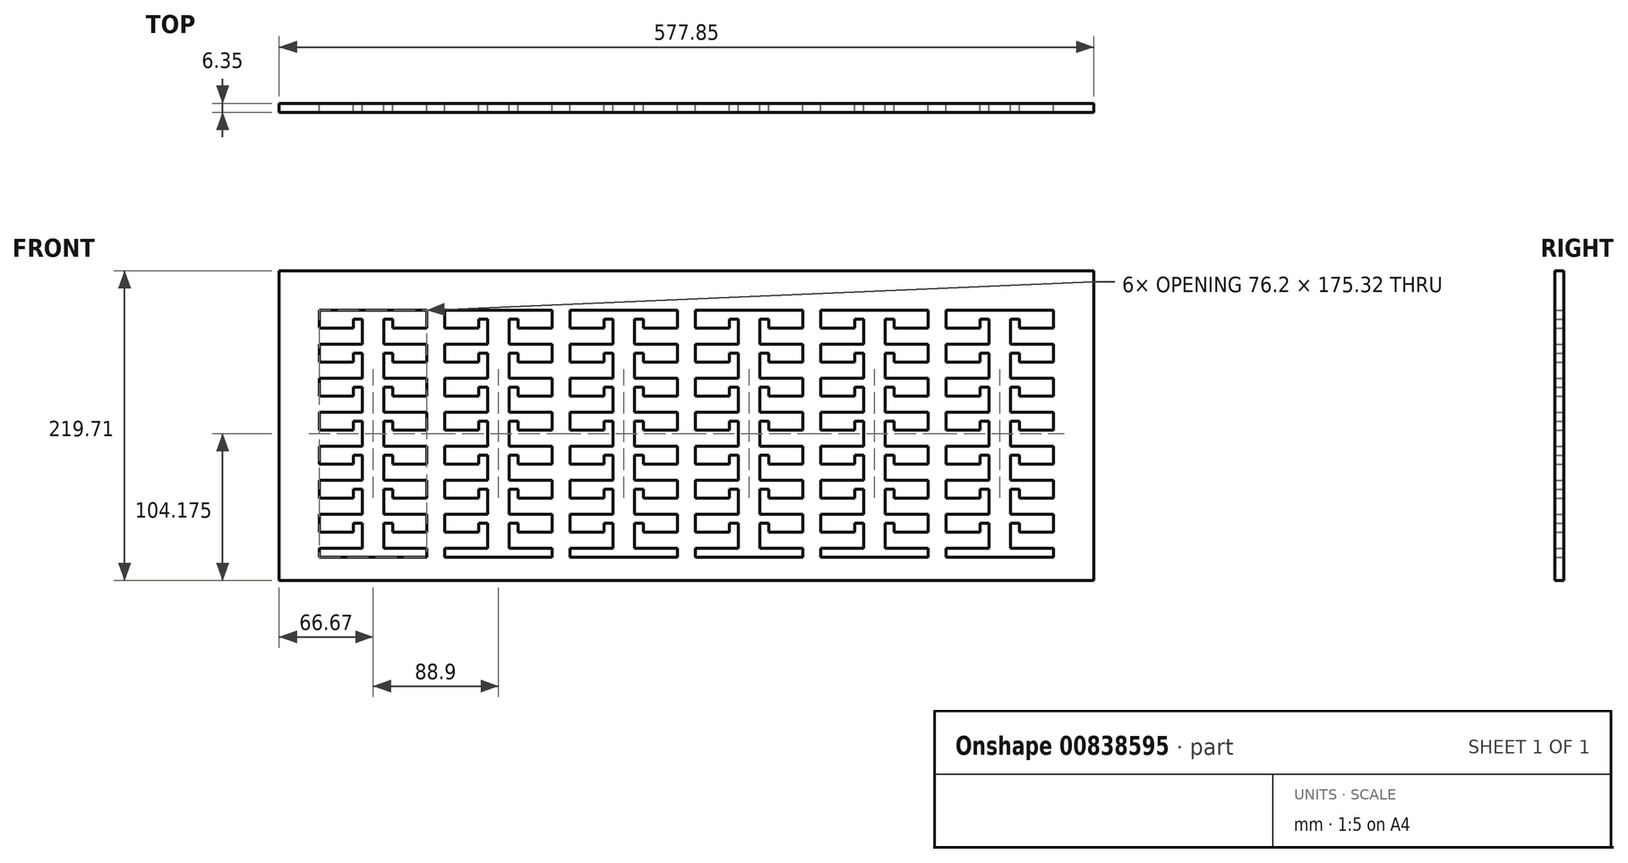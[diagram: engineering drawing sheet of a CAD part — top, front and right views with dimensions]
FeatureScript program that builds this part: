
annotation { "Feature Type Name" : "Feature", "Feature Type Description" : "" }
export const myFeature = defineFeature(function(context is Context, id is Id, definition is map)
    precondition{}
    {
        {
            var Q0;
            Q0=qCreatedBy(makeId("Front.planeOp"),FACE);
            var sketch = newSketch(context, id + "F0", { "sketchPlane" : qUnion([Q0])});
            skLineSegment(sketch, "E0", {"start": v(-97.96, -49.5) * mm, "end": v(-67.48, -49.5) * mm});
            skLineSegment(sketch, "E1", {"start": v(-67.48, -49.5) * mm, "end": v(-67.48, -31.72) * mm});
            skLineSegment(sketch, "E2", {"start": v(-67.48, -31.72) * mm, "end": v(-73.83, -31.72) * mm});
            skLineSegment(sketch, "E3", {"start": v(-73.83, -31.72) * mm, "end": v(-73.83, -38.07) * mm});
            skLineSegment(sketch, "E4", {"start": v(-73.83, -38.07) * mm, "end": v(-97.96, -38.07) * mm});
            skLineSegment(sketch, "E5", {"start": v(-97.96, -38.07) * mm, "end": v(-97.96, -25.37) * mm});
            skLineSegment(sketch, "E6", {"start": v(-97.96, -25.37) * mm, "end": v(-67.48, -25.37) * mm});
            skLineSegment(sketch, "E7", {"start": v(-67.48, -25.37) * mm, "end": v(-67.48, -7.6) * mm});
            skLineSegment(sketch, "E8", {"start": v(-67.48, -7.6) * mm, "end": v(-73.83, -7.6) * mm});
            skLineSegment(sketch, "E9", {"start": v(-73.83, -7.6) * mm, "end": v(-73.83, -13.94) * mm});
            skLineSegment(sketch, "E10", {"start": v(-73.83, -13.94) * mm, "end": v(-97.96, -13.94) * mm});
            skLineSegment(sketch, "E11", {"start": v(-97.96, -13.94) * mm, "end": v(-97.96, -1.24) * mm});
            skLineSegment(sketch, "E12", {"start": v(-97.96, -1.24) * mm, "end": v(-67.48, -1.24) * mm});
            skLineSegment(sketch, "E13", {"start": v(-67.48, -1.24) * mm, "end": v(-67.48, 16.54) * mm});
            skLineSegment(sketch, "E14", {"start": v(-67.48, 16.54) * mm, "end": v(-73.83, 16.54) * mm});
            skLineSegment(sketch, "E15", {"start": v(-73.83, 16.54) * mm, "end": v(-73.83, 10.19) * mm});
            skLineSegment(sketch, "E16", {"start": v(-73.83, 10.19) * mm, "end": v(-97.96, 10.19) * mm});
            skLineSegment(sketch, "E17", {"start": v(-97.96, 10.19) * mm, "end": v(-97.96, 22.89) * mm});
            skLineSegment(sketch, "E18", {"start": v(-97.96, 22.89) * mm, "end": v(-67.48, 22.89) * mm});
            skLineSegment(sketch, "E19", {"start": v(-67.48, 22.89) * mm, "end": v(-67.48, 40.67) * mm});
            skLineSegment(sketch, "E20", {"start": v(-67.48, 40.67) * mm, "end": v(-73.83, 40.67) * mm});
            skLineSegment(sketch, "E21", {"start": v(-73.83, 40.67) * mm, "end": v(-73.83, 34.32) * mm});
            skLineSegment(sketch, "E22", {"start": v(-73.83, 34.32) * mm, "end": v(-97.96, 34.32) * mm});
            skLineSegment(sketch, "E23", {"start": v(-97.96, 34.32) * mm, "end": v(-97.96, 47.02) * mm});
            skLineSegment(sketch, "E24", {"start": v(-21.76, -80.05) * mm, "end": v(-21.76, -73.63) * mm});
            skLineSegment(sketch, "E25", {"start": v(-21.76, -73.63) * mm, "end": v(-52.24, -73.63) * mm});
            skLineSegment(sketch, "E26", {"start": v(-52.24, -73.63) * mm, "end": v(-52.24, -55.85) * mm});
            skLineSegment(sketch, "E27", {"start": v(-52.24, -55.85) * mm, "end": v(-45.89, -55.85) * mm});
            skLineSegment(sketch, "E28", {"start": v(-45.89, -55.85) * mm, "end": v(-45.89, -62.2) * mm});
            skLineSegment(sketch, "E29", {"start": v(-45.89, -62.2) * mm, "end": v(-21.76, -62.2) * mm});
            skLineSegment(sketch, "E30", {"start": v(-21.76, -62.2) * mm, "end": v(-21.76, -49.5) * mm});
            skLineSegment(sketch, "E31", {"start": v(-21.76, -49.5) * mm, "end": v(-52.24, -49.5) * mm});
            skLineSegment(sketch, "E32", {"start": v(-52.24, -49.5) * mm, "end": v(-52.24, -31.72) * mm});
            skLineSegment(sketch, "E33", {"start": v(-52.24, -31.72) * mm, "end": v(-45.89, -31.72) * mm});
            skLineSegment(sketch, "E34", {"start": v(-45.89, -31.72) * mm, "end": v(-45.89, -38.07) * mm});
            skLineSegment(sketch, "E35", {"start": v(-45.89, -38.07) * mm, "end": v(-21.76, -38.07) * mm});
            skLineSegment(sketch, "E36", {"start": v(-21.76, -38.07) * mm, "end": v(-21.76, -25.37) * mm});
            skLineSegment(sketch, "E37", {"start": v(-21.76, -25.37) * mm, "end": v(-52.24, -25.37) * mm});
            skLineSegment(sketch, "E38", {"start": v(-52.24, -25.37) * mm, "end": v(-52.24, -7.6) * mm});
            skLineSegment(sketch, "E39", {"start": v(-52.24, -7.6) * mm, "end": v(-45.89, -7.6) * mm});
            skLineSegment(sketch, "E40", {"start": v(-45.89, -7.6) * mm, "end": v(-45.89, -13.94) * mm});
            skLineSegment(sketch, "E41", {"start": v(-45.89, -13.94) * mm, "end": v(-21.76, -13.94) * mm});
            skLineSegment(sketch, "E42", {"start": v(-21.76, -13.94) * mm, "end": v(-21.76, -1.24) * mm});
            skLineSegment(sketch, "E43", {"start": v(-21.76, -1.24) * mm, "end": v(-52.24, -1.24) * mm});
            skLineSegment(sketch, "E44", {"start": v(-52.24, -1.24) * mm, "end": v(-52.24, 16.54) * mm});
            skLineSegment(sketch, "E45", {"start": v(-52.24, 16.54) * mm, "end": v(-45.89, 16.54) * mm});
            skLineSegment(sketch, "E46", {"start": v(-45.89, 16.54) * mm, "end": v(-45.89, 10.19) * mm});
            skLineSegment(sketch, "E47", {"start": v(-45.89, 10.19) * mm, "end": v(-21.76, 10.19) * mm});
            skLineSegment(sketch, "E48", {"start": v(-21.76, 10.19) * mm, "end": v(-21.76, 22.89) * mm});
            skLineSegment(sketch, "E49", {"start": v(-21.76, 22.89) * mm, "end": v(-52.24, 22.89) * mm});
            skLineSegment(sketch, "E50", {"start": v(-52.24, 22.89) * mm, "end": v(-52.24, 40.67) * mm});
            skLineSegment(sketch, "E51", {"start": v(-52.24, 40.67) * mm, "end": v(-45.89, 40.67) * mm});
            skLineSegment(sketch, "E52", {"start": v(-45.89, 40.67) * mm, "end": v(-45.89, 34.32) * mm});
            skLineSegment(sketch, "E53", {"start": v(-45.89, 34.32) * mm, "end": v(-21.76, 34.32) * mm});
            skLineSegment(sketch, "E54", {"start": v(-21.76, 34.32) * mm, "end": v(-21.76, 47.02) * mm});
            skLineSegment(sketch, "E55", {"start": v(-67.48, -73.63) * mm, "end": v(-67.48, -55.85) * mm});
            skLineSegment(sketch, "E56", {"start": v(-73.83, -62.2) * mm, "end": v(-73.83, -55.85) * mm});
            skLineSegment(sketch, "E57", {"start": v(-73.83, -55.85) * mm, "end": v(-67.48, -55.85) * mm});
            skLineSegment(sketch, "E58", {"start": v(-67.48, -73.63) * mm, "end": v(-97.96, -73.63) * mm});
            skLineSegment(sketch, "E59", {"start": v(-97.96, -62.2) * mm, "end": v(-97.96, -49.5) * mm});
            skLineSegment(sketch, "E60", {"start": v(-97.96, -73.63) * mm, "end": v(-97.96, -80.05) * mm});
            skLineSegment(sketch, "E61", {"start": v(-97.96, -62.2) * mm, "end": v(-73.83, -62.2) * mm});
            skLineSegment(sketch, "E62", {"start": v(-97.96, -80.05) * mm, "end": v(-21.76, -80.05) * mm});
            skPoint(sketch, "E63", {"position": v(-59.86, -80.05) * mm});
            skLineSegment(sketch, "E64", {"start": v(-186.86, -49.5) * mm, "end": v(-156.38, -49.5) * mm});
            skLineSegment(sketch, "E65", {"start": v(-156.38, -49.5) * mm, "end": v(-156.38, -31.72) * mm});
            skLineSegment(sketch, "E66", {"start": v(-156.38, -31.72) * mm, "end": v(-162.73, -31.72) * mm});
            skLineSegment(sketch, "E67", {"start": v(-162.73, -31.72) * mm, "end": v(-162.73, -38.07) * mm});
            skLineSegment(sketch, "E68", {"start": v(-162.73, -38.07) * mm, "end": v(-186.86, -38.07) * mm});
            skLineSegment(sketch, "E69", {"start": v(-186.86, -38.07) * mm, "end": v(-186.86, -25.37) * mm});
            skLineSegment(sketch, "E70", {"start": v(-186.86, -25.37) * mm, "end": v(-156.38, -25.37) * mm});
            skLineSegment(sketch, "E71", {"start": v(-156.38, -25.37) * mm, "end": v(-156.38, -7.6) * mm});
            skLineSegment(sketch, "E72", {"start": v(-156.38, -7.6) * mm, "end": v(-162.73, -7.6) * mm});
            skLineSegment(sketch, "E73", {"start": v(-162.73, -7.6) * mm, "end": v(-162.73, -13.94) * mm});
            skLineSegment(sketch, "E74", {"start": v(-162.73, -13.94) * mm, "end": v(-186.86, -13.94) * mm});
            skLineSegment(sketch, "E75", {"start": v(-186.86, -13.94) * mm, "end": v(-186.86, -1.24) * mm});
            skLineSegment(sketch, "E76", {"start": v(-186.86, -1.24) * mm, "end": v(-156.38, -1.24) * mm});
            skLineSegment(sketch, "E77", {"start": v(-156.38, -1.24) * mm, "end": v(-156.38, 16.54) * mm});
            skLineSegment(sketch, "E78", {"start": v(-156.38, 16.54) * mm, "end": v(-162.73, 16.54) * mm});
            skLineSegment(sketch, "E79", {"start": v(-162.73, 16.54) * mm, "end": v(-162.73, 10.19) * mm});
            skLineSegment(sketch, "E80", {"start": v(-162.73, 10.19) * mm, "end": v(-186.86, 10.19) * mm});
            skLineSegment(sketch, "E81", {"start": v(-186.86, 10.19) * mm, "end": v(-186.86, 22.89) * mm});
            skLineSegment(sketch, "E82", {"start": v(-186.86, 22.89) * mm, "end": v(-156.38, 22.89) * mm});
            skLineSegment(sketch, "E83", {"start": v(-156.38, 22.89) * mm, "end": v(-156.38, 40.67) * mm});
            skLineSegment(sketch, "E84", {"start": v(-156.38, 40.67) * mm, "end": v(-162.73, 40.67) * mm});
            skLineSegment(sketch, "E85", {"start": v(-162.73, 40.67) * mm, "end": v(-162.73, 34.32) * mm});
            skLineSegment(sketch, "E86", {"start": v(-162.73, 34.32) * mm, "end": v(-186.86, 34.32) * mm});
            skLineSegment(sketch, "E87", {"start": v(-186.86, 34.32) * mm, "end": v(-186.86, 47.02) * mm});
            skLineSegment(sketch, "E88", {"start": v(-110.66, -80.05) * mm, "end": v(-110.66, -73.63) * mm});
            skLineSegment(sketch, "E89", {"start": v(-110.66, -73.63) * mm, "end": v(-141.14, -73.63) * mm});
            skLineSegment(sketch, "E90", {"start": v(-141.14, -73.63) * mm, "end": v(-141.14, -55.85) * mm});
            skLineSegment(sketch, "E91", {"start": v(-141.14, -55.85) * mm, "end": v(-134.79, -55.85) * mm});
            skLineSegment(sketch, "E92", {"start": v(-134.79, -55.85) * mm, "end": v(-134.79, -62.2) * mm});
            skLineSegment(sketch, "E93", {"start": v(-134.79, -62.2) * mm, "end": v(-110.66, -62.2) * mm});
            skLineSegment(sketch, "E94", {"start": v(-110.66, -62.2) * mm, "end": v(-110.66, -49.5) * mm});
            skLineSegment(sketch, "E95", {"start": v(-110.66, -49.5) * mm, "end": v(-141.14, -49.5) * mm});
            skLineSegment(sketch, "E96", {"start": v(-141.14, -49.5) * mm, "end": v(-141.14, -31.72) * mm});
            skLineSegment(sketch, "E97", {"start": v(-141.14, -31.72) * mm, "end": v(-134.79, -31.72) * mm});
            skLineSegment(sketch, "E98", {"start": v(-134.79, -31.72) * mm, "end": v(-134.79, -38.07) * mm});
            skLineSegment(sketch, "E99", {"start": v(-134.79, -38.07) * mm, "end": v(-110.66, -38.07) * mm});
            skLineSegment(sketch, "E100", {"start": v(-110.66, -38.07) * mm, "end": v(-110.66, -25.37) * mm});
            skLineSegment(sketch, "E101", {"start": v(-110.66, -25.37) * mm, "end": v(-141.14, -25.37) * mm});
            skLineSegment(sketch, "E102", {"start": v(-141.14, -25.37) * mm, "end": v(-141.14, -7.6) * mm});
            skLineSegment(sketch, "E103", {"start": v(-141.14, -7.6) * mm, "end": v(-134.79, -7.6) * mm});
            skLineSegment(sketch, "E104", {"start": v(-134.79, -7.6) * mm, "end": v(-134.79, -13.94) * mm});
            skLineSegment(sketch, "E105", {"start": v(-134.79, -13.94) * mm, "end": v(-110.66, -13.94) * mm});
            skLineSegment(sketch, "E106", {"start": v(-110.66, -13.94) * mm, "end": v(-110.66, -1.24) * mm});
            skLineSegment(sketch, "E107", {"start": v(-110.66, -1.24) * mm, "end": v(-141.14, -1.24) * mm});
            skLineSegment(sketch, "E108", {"start": v(-141.14, -1.24) * mm, "end": v(-141.14, 16.54) * mm});
            skLineSegment(sketch, "E109", {"start": v(-141.14, 16.54) * mm, "end": v(-134.79, 16.54) * mm});
            skLineSegment(sketch, "E110", {"start": v(-134.79, 16.54) * mm, "end": v(-134.79, 10.19) * mm});
            skLineSegment(sketch, "E111", {"start": v(-134.79, 10.19) * mm, "end": v(-110.66, 10.19) * mm});
            skLineSegment(sketch, "E112", {"start": v(-110.66, 10.19) * mm, "end": v(-110.66, 22.89) * mm});
            skLineSegment(sketch, "E113", {"start": v(-110.66, 22.89) * mm, "end": v(-141.14, 22.89) * mm});
            skLineSegment(sketch, "E114", {"start": v(-141.14, 22.89) * mm, "end": v(-141.14, 40.67) * mm});
            skLineSegment(sketch, "E115", {"start": v(-141.14, 40.67) * mm, "end": v(-134.79, 40.67) * mm});
            skLineSegment(sketch, "E116", {"start": v(-134.79, 40.67) * mm, "end": v(-134.79, 34.32) * mm});
            skLineSegment(sketch, "E117", {"start": v(-134.79, 34.32) * mm, "end": v(-110.66, 34.32) * mm});
            skLineSegment(sketch, "E118", {"start": v(-110.66, 34.32) * mm, "end": v(-110.66, 47.02) * mm});
            skLineSegment(sketch, "E119", {"start": v(-156.38, -73.63) * mm, "end": v(-156.38, -55.85) * mm});
            skLineSegment(sketch, "E120", {"start": v(-162.73, -62.2) * mm, "end": v(-162.73, -55.85) * mm});
            skLineSegment(sketch, "E121", {"start": v(-162.73, -55.85) * mm, "end": v(-156.38, -55.85) * mm});
            skLineSegment(sketch, "E122", {"start": v(-156.38, -73.63) * mm, "end": v(-186.86, -73.63) * mm});
            skLineSegment(sketch, "E123", {"start": v(-186.86, -62.2) * mm, "end": v(-186.86, -49.5) * mm});
            skLineSegment(sketch, "E124", {"start": v(-186.86, -73.63) * mm, "end": v(-186.86, -80.05) * mm});
            skLineSegment(sketch, "E125", {"start": v(-186.86, -62.2) * mm, "end": v(-162.73, -62.2) * mm});
            skLineSegment(sketch, "E126", {"start": v(-186.86, -80.05) * mm, "end": v(-110.66, -80.05) * mm});
            skPoint(sketch, "E127", {"position": v(-148.76, -80.05) * mm});
            skLineSegment(sketch, "E128", {"start": v(-275.76, -49.5) * mm, "end": v(-245.28, -49.5) * mm});
            skLineSegment(sketch, "E129", {"start": v(-245.28, -49.5) * mm, "end": v(-245.28, -31.72) * mm});
            skLineSegment(sketch, "E130", {"start": v(-245.28, -31.72) * mm, "end": v(-251.63, -31.72) * mm});
            skLineSegment(sketch, "E131", {"start": v(-251.63, -31.72) * mm, "end": v(-251.63, -38.07) * mm});
            skLineSegment(sketch, "E132", {"start": v(-251.63, -38.07) * mm, "end": v(-275.76, -38.07) * mm});
            skLineSegment(sketch, "E133", {"start": v(-275.76, -38.07) * mm, "end": v(-275.76, -25.37) * mm});
            skLineSegment(sketch, "E134", {"start": v(-275.76, -25.37) * mm, "end": v(-245.28, -25.37) * mm});
            skLineSegment(sketch, "E135", {"start": v(-245.28, -25.37) * mm, "end": v(-245.28, -7.6) * mm});
            skLineSegment(sketch, "E136", {"start": v(-245.28, -7.6) * mm, "end": v(-251.63, -7.6) * mm});
            skLineSegment(sketch, "E137", {"start": v(-251.63, -7.6) * mm, "end": v(-251.63, -13.94) * mm});
            skLineSegment(sketch, "E138", {"start": v(-251.63, -13.94) * mm, "end": v(-275.76, -13.94) * mm});
            skLineSegment(sketch, "E139", {"start": v(-275.76, -13.94) * mm, "end": v(-275.76, -1.24) * mm});
            skLineSegment(sketch, "E140", {"start": v(-275.76, -1.24) * mm, "end": v(-245.28, -1.24) * mm});
            skLineSegment(sketch, "E141", {"start": v(-245.28, -1.24) * mm, "end": v(-245.28, 16.54) * mm});
            skLineSegment(sketch, "E142", {"start": v(-245.28, 16.54) * mm, "end": v(-251.63, 16.54) * mm});
            skLineSegment(sketch, "E143", {"start": v(-251.63, 16.54) * mm, "end": v(-251.63, 10.19) * mm});
            skLineSegment(sketch, "E144", {"start": v(-251.63, 10.19) * mm, "end": v(-275.76, 10.19) * mm});
            skLineSegment(sketch, "E145", {"start": v(-275.76, 10.19) * mm, "end": v(-275.76, 22.89) * mm});
            skLineSegment(sketch, "E146", {"start": v(-275.76, 22.89) * mm, "end": v(-245.28, 22.89) * mm});
            skLineSegment(sketch, "E147", {"start": v(-245.28, 22.89) * mm, "end": v(-245.28, 40.67) * mm});
            skLineSegment(sketch, "E148", {"start": v(-245.28, 40.67) * mm, "end": v(-251.63, 40.67) * mm});
            skLineSegment(sketch, "E149", {"start": v(-251.63, 40.67) * mm, "end": v(-251.63, 34.32) * mm});
            skLineSegment(sketch, "E150", {"start": v(-251.63, 34.32) * mm, "end": v(-275.76, 34.32) * mm});
            skLineSegment(sketch, "E151", {"start": v(-275.76, 34.32) * mm, "end": v(-275.76, 47.02) * mm});
            skLineSegment(sketch, "E152", {"start": v(-199.56, -80.05) * mm, "end": v(-199.56, -73.63) * mm});
            skLineSegment(sketch, "E153", {"start": v(-199.56, -73.63) * mm, "end": v(-230.04, -73.63) * mm});
            skLineSegment(sketch, "E154", {"start": v(-230.04, -73.63) * mm, "end": v(-230.04, -55.85) * mm});
            skLineSegment(sketch, "E155", {"start": v(-230.04, -55.85) * mm, "end": v(-223.69, -55.85) * mm});
            skLineSegment(sketch, "E156", {"start": v(-223.69, -55.85) * mm, "end": v(-223.69, -62.2) * mm});
            skLineSegment(sketch, "E157", {"start": v(-223.69, -62.2) * mm, "end": v(-199.56, -62.2) * mm});
            skLineSegment(sketch, "E158", {"start": v(-199.56, -62.2) * mm, "end": v(-199.56, -49.5) * mm});
            skLineSegment(sketch, "E159", {"start": v(-199.56, -49.5) * mm, "end": v(-230.04, -49.5) * mm});
            skLineSegment(sketch, "E160", {"start": v(-230.04, -49.5) * mm, "end": v(-230.04, -31.72) * mm});
            skLineSegment(sketch, "E161", {"start": v(-230.04, -31.72) * mm, "end": v(-223.69, -31.72) * mm});
            skLineSegment(sketch, "E162", {"start": v(-223.69, -31.72) * mm, "end": v(-223.69, -38.07) * mm});
            skLineSegment(sketch, "E163", {"start": v(-223.69, -38.07) * mm, "end": v(-199.56, -38.07) * mm});
            skLineSegment(sketch, "E164", {"start": v(-199.56, -38.07) * mm, "end": v(-199.56, -25.37) * mm});
            skLineSegment(sketch, "E165", {"start": v(-199.56, -25.37) * mm, "end": v(-230.04, -25.37) * mm});
            skLineSegment(sketch, "E166", {"start": v(-230.04, -25.37) * mm, "end": v(-230.04, -7.6) * mm});
            skLineSegment(sketch, "E167", {"start": v(-230.04, -7.6) * mm, "end": v(-223.69, -7.6) * mm});
            skLineSegment(sketch, "E168", {"start": v(-223.69, -7.6) * mm, "end": v(-223.69, -13.94) * mm});
            skLineSegment(sketch, "E169", {"start": v(-223.69, -13.94) * mm, "end": v(-199.56, -13.94) * mm});
            skLineSegment(sketch, "E170", {"start": v(-199.56, -13.94) * mm, "end": v(-199.56, -1.24) * mm});
            skLineSegment(sketch, "E171", {"start": v(-199.56, -1.24) * mm, "end": v(-230.04, -1.24) * mm});
            skLineSegment(sketch, "E172", {"start": v(-230.04, -1.24) * mm, "end": v(-230.04, 16.54) * mm});
            skLineSegment(sketch, "E173", {"start": v(-230.04, 16.54) * mm, "end": v(-223.69, 16.54) * mm});
            skLineSegment(sketch, "E174", {"start": v(-223.69, 16.54) * mm, "end": v(-223.69, 10.19) * mm});
            skLineSegment(sketch, "E175", {"start": v(-223.69, 10.19) * mm, "end": v(-199.56, 10.19) * mm});
            skLineSegment(sketch, "E176", {"start": v(-199.56, 10.19) * mm, "end": v(-199.56, 22.89) * mm});
            skLineSegment(sketch, "E177", {"start": v(-199.56, 22.89) * mm, "end": v(-230.04, 22.89) * mm});
            skLineSegment(sketch, "E178", {"start": v(-230.04, 22.89) * mm, "end": v(-230.04, 40.67) * mm});
            skLineSegment(sketch, "E179", {"start": v(-230.04, 40.67) * mm, "end": v(-223.69, 40.67) * mm});
            skLineSegment(sketch, "E180", {"start": v(-223.69, 40.67) * mm, "end": v(-223.69, 34.32) * mm});
            skLineSegment(sketch, "E181", {"start": v(-223.69, 34.32) * mm, "end": v(-199.56, 34.32) * mm});
            skLineSegment(sketch, "E182", {"start": v(-199.56, 34.32) * mm, "end": v(-199.56, 47.02) * mm});
            skLineSegment(sketch, "E183", {"start": v(-245.28, -73.63) * mm, "end": v(-245.28, -55.85) * mm});
            skLineSegment(sketch, "E184", {"start": v(-251.63, -62.2) * mm, "end": v(-251.63, -55.85) * mm});
            skLineSegment(sketch, "E185", {"start": v(-251.63, -55.85) * mm, "end": v(-245.28, -55.85) * mm});
            skLineSegment(sketch, "E186", {"start": v(-245.28, -73.63) * mm, "end": v(-275.76, -73.63) * mm});
            skLineSegment(sketch, "E187", {"start": v(-275.76, -62.2) * mm, "end": v(-275.76, -49.5) * mm});
            skLineSegment(sketch, "E188", {"start": v(-275.76, -73.63) * mm, "end": v(-275.76, -80.05) * mm});
            skLineSegment(sketch, "E189", {"start": v(-275.76, -62.2) * mm, "end": v(-251.63, -62.2) * mm});
            skLineSegment(sketch, "E190", {"start": v(-275.76, -80.05) * mm, "end": v(-199.56, -80.05) * mm});
            skPoint(sketch, "E191", {"position": v(-237.66, -80.05) * mm});
            skLineSegment(sketch, "E192", {"start": v(-364.66, -49.5) * mm, "end": v(-334.18, -49.5) * mm});
            skLineSegment(sketch, "E193", {"start": v(-334.18, -49.5) * mm, "end": v(-334.18, -31.72) * mm});
            skLineSegment(sketch, "E194", {"start": v(-334.18, -31.72) * mm, "end": v(-340.53, -31.72) * mm});
            skLineSegment(sketch, "E195", {"start": v(-340.53, -31.72) * mm, "end": v(-340.53, -38.07) * mm});
            skLineSegment(sketch, "E196", {"start": v(-340.53, -38.07) * mm, "end": v(-364.66, -38.07) * mm});
            skLineSegment(sketch, "E197", {"start": v(-364.66, -38.07) * mm, "end": v(-364.66, -25.37) * mm});
            skLineSegment(sketch, "E198", {"start": v(-364.66, -25.37) * mm, "end": v(-334.18, -25.37) * mm});
            skLineSegment(sketch, "E199", {"start": v(-334.18, -25.37) * mm, "end": v(-334.18, -7.6) * mm});
            skLineSegment(sketch, "E200", {"start": v(-334.18, -7.6) * mm, "end": v(-340.53, -7.6) * mm});
            skLineSegment(sketch, "E201", {"start": v(-340.53, -7.6) * mm, "end": v(-340.53, -13.94) * mm});
            skLineSegment(sketch, "E202", {"start": v(-340.53, -13.94) * mm, "end": v(-364.66, -13.94) * mm});
            skLineSegment(sketch, "E203", {"start": v(-364.66, -13.94) * mm, "end": v(-364.66, -1.24) * mm});
            skLineSegment(sketch, "E204", {"start": v(-364.66, -1.24) * mm, "end": v(-334.18, -1.24) * mm});
            skLineSegment(sketch, "E205", {"start": v(-334.18, -1.24) * mm, "end": v(-334.18, 16.54) * mm});
            skLineSegment(sketch, "E206", {"start": v(-334.18, 16.54) * mm, "end": v(-340.53, 16.54) * mm});
            skLineSegment(sketch, "E207", {"start": v(-340.53, 16.54) * mm, "end": v(-340.53, 10.19) * mm});
            skLineSegment(sketch, "E208", {"start": v(-340.53, 10.19) * mm, "end": v(-364.66, 10.19) * mm});
            skLineSegment(sketch, "E209", {"start": v(-364.66, 10.19) * mm, "end": v(-364.66, 22.89) * mm});
            skLineSegment(sketch, "E210", {"start": v(-364.66, 22.89) * mm, "end": v(-334.18, 22.89) * mm});
            skLineSegment(sketch, "E211", {"start": v(-334.18, 22.89) * mm, "end": v(-334.18, 40.67) * mm});
            skLineSegment(sketch, "E212", {"start": v(-334.18, 40.67) * mm, "end": v(-340.53, 40.67) * mm});
            skLineSegment(sketch, "E213", {"start": v(-340.53, 40.67) * mm, "end": v(-340.53, 34.32) * mm});
            skLineSegment(sketch, "E214", {"start": v(-340.53, 34.32) * mm, "end": v(-364.66, 34.32) * mm});
            skLineSegment(sketch, "E215", {"start": v(-364.66, 34.32) * mm, "end": v(-364.66, 47.02) * mm});
            skLineSegment(sketch, "E216", {"start": v(-288.46, -80.05) * mm, "end": v(-288.46, -73.63) * mm});
            skLineSegment(sketch, "E217", {"start": v(-288.46, -73.63) * mm, "end": v(-318.94, -73.63) * mm});
            skLineSegment(sketch, "E218", {"start": v(-318.94, -73.63) * mm, "end": v(-318.94, -55.85) * mm});
            skLineSegment(sketch, "E219", {"start": v(-318.94, -55.85) * mm, "end": v(-312.59, -55.85) * mm});
            skLineSegment(sketch, "E220", {"start": v(-312.59, -55.85) * mm, "end": v(-312.59, -62.2) * mm});
            skLineSegment(sketch, "E221", {"start": v(-312.59, -62.2) * mm, "end": v(-288.46, -62.2) * mm});
            skLineSegment(sketch, "E222", {"start": v(-288.46, -62.2) * mm, "end": v(-288.46, -49.5) * mm});
            skLineSegment(sketch, "E223", {"start": v(-288.46, -49.5) * mm, "end": v(-318.94, -49.5) * mm});
            skLineSegment(sketch, "E224", {"start": v(-318.94, -49.5) * mm, "end": v(-318.94, -31.72) * mm});
            skLineSegment(sketch, "E225", {"start": v(-318.94, -31.72) * mm, "end": v(-312.59, -31.72) * mm});
            skLineSegment(sketch, "E226", {"start": v(-312.59, -31.72) * mm, "end": v(-312.59, -38.07) * mm});
            skLineSegment(sketch, "E227", {"start": v(-312.59, -38.07) * mm, "end": v(-288.46, -38.07) * mm});
            skLineSegment(sketch, "E228", {"start": v(-288.46, -38.07) * mm, "end": v(-288.46, -25.37) * mm});
            skLineSegment(sketch, "E229", {"start": v(-288.46, -25.37) * mm, "end": v(-318.94, -25.37) * mm});
            skLineSegment(sketch, "E230", {"start": v(-318.94, -25.37) * mm, "end": v(-318.94, -7.6) * mm});
            skLineSegment(sketch, "E231", {"start": v(-318.94, -7.6) * mm, "end": v(-312.59, -7.6) * mm});
            skLineSegment(sketch, "E232", {"start": v(-312.59, -7.6) * mm, "end": v(-312.59, -13.94) * mm});
            skLineSegment(sketch, "E233", {"start": v(-312.59, -13.94) * mm, "end": v(-288.46, -13.94) * mm});
            skLineSegment(sketch, "E234", {"start": v(-288.46, -13.94) * mm, "end": v(-288.46, -1.24) * mm});
            skLineSegment(sketch, "E235", {"start": v(-288.46, -1.24) * mm, "end": v(-318.94, -1.24) * mm});
            skLineSegment(sketch, "E236", {"start": v(-318.94, -1.24) * mm, "end": v(-318.94, 16.54) * mm});
            skLineSegment(sketch, "E237", {"start": v(-318.94, 16.54) * mm, "end": v(-312.59, 16.54) * mm});
            skLineSegment(sketch, "E238", {"start": v(-312.59, 16.54) * mm, "end": v(-312.59, 10.19) * mm});
            skLineSegment(sketch, "E239", {"start": v(-312.59, 10.19) * mm, "end": v(-288.46, 10.19) * mm});
            skLineSegment(sketch, "E240", {"start": v(-288.46, 10.19) * mm, "end": v(-288.46, 22.89) * mm});
            skLineSegment(sketch, "E241", {"start": v(-288.46, 22.89) * mm, "end": v(-318.94, 22.89) * mm});
            skLineSegment(sketch, "E242", {"start": v(-318.94, 22.89) * mm, "end": v(-318.94, 40.67) * mm});
            skLineSegment(sketch, "E243", {"start": v(-318.94, 40.67) * mm, "end": v(-312.59, 40.67) * mm});
            skLineSegment(sketch, "E244", {"start": v(-312.59, 40.67) * mm, "end": v(-312.59, 34.32) * mm});
            skLineSegment(sketch, "E245", {"start": v(-312.59, 34.32) * mm, "end": v(-288.46, 34.32) * mm});
            skLineSegment(sketch, "E246", {"start": v(-288.46, 34.32) * mm, "end": v(-288.46, 47.02) * mm});
            skLineSegment(sketch, "E247", {"start": v(-334.18, -73.63) * mm, "end": v(-334.18, -55.85) * mm});
            skLineSegment(sketch, "E248", {"start": v(-340.53, -62.2) * mm, "end": v(-340.53, -55.85) * mm});
            skLineSegment(sketch, "E249", {"start": v(-340.53, -55.85) * mm, "end": v(-334.18, -55.85) * mm});
            skLineSegment(sketch, "E250", {"start": v(-334.18, -73.63) * mm, "end": v(-364.66, -73.63) * mm});
            skLineSegment(sketch, "E251", {"start": v(-364.66, -62.2) * mm, "end": v(-364.66, -49.5) * mm});
            skLineSegment(sketch, "E252", {"start": v(-364.66, -73.63) * mm, "end": v(-364.66, -80.05) * mm});
            skLineSegment(sketch, "E253", {"start": v(-364.66, -62.2) * mm, "end": v(-340.53, -62.2) * mm});
            skLineSegment(sketch, "E254", {"start": v(-364.66, -80.05) * mm, "end": v(-288.46, -80.05) * mm});
            skPoint(sketch, "E255", {"position": v(-326.56, -80.05) * mm});
            skLineSegment(sketch, "E256.bottom", {"start": v(6.82, 123.15) * mm, "end": v(-571.03, 123.15) * mm});
            skLineSegment(sketch, "E256.top", {"start": v(6.82, -96.56) * mm, "end": v(-571.03, -96.56) * mm});
            skLineSegment(sketch, "E256.left", {"start": v(6.82, 123.15) * mm, "end": v(6.82, -96.56) * mm});
            skLineSegment(sketch, "E256.right", {"start": v(-571.03, 123.15) * mm, "end": v(-571.03, -96.56) * mm});
            skPoint(sketch, "E257", {"position": v(-282.1, 123.15) * mm});
            skLineSegment(sketch, "E258", {"start": v(-453.56, -49.5) * mm, "end": v(-423.08, -49.5) * mm});
            skLineSegment(sketch, "E259", {"start": v(-423.08, -49.5) * mm, "end": v(-423.08, -31.72) * mm});
            skLineSegment(sketch, "E260", {"start": v(-423.08, -31.72) * mm, "end": v(-429.43, -31.72) * mm});
            skLineSegment(sketch, "E261", {"start": v(-429.43, -31.72) * mm, "end": v(-429.43, -38.07) * mm});
            skLineSegment(sketch, "E262", {"start": v(-429.43, -38.07) * mm, "end": v(-453.56, -38.07) * mm});
            skLineSegment(sketch, "E263", {"start": v(-453.56, -38.07) * mm, "end": v(-453.56, -25.37) * mm});
            skLineSegment(sketch, "E264", {"start": v(-453.56, -25.37) * mm, "end": v(-423.08, -25.37) * mm});
            skLineSegment(sketch, "E265", {"start": v(-423.08, -25.37) * mm, "end": v(-423.08, -7.6) * mm});
            skLineSegment(sketch, "E266", {"start": v(-423.08, -7.6) * mm, "end": v(-429.43, -7.6) * mm});
            skLineSegment(sketch, "E267", {"start": v(-429.43, -7.6) * mm, "end": v(-429.43, -13.94) * mm});
            skLineSegment(sketch, "E268", {"start": v(-429.43, -13.94) * mm, "end": v(-453.56, -13.94) * mm});
            skLineSegment(sketch, "E269", {"start": v(-453.56, -13.94) * mm, "end": v(-453.56, -1.24) * mm});
            skLineSegment(sketch, "E270", {"start": v(-453.56, -1.24) * mm, "end": v(-423.08, -1.24) * mm});
            skLineSegment(sketch, "E271", {"start": v(-423.08, -1.24) * mm, "end": v(-423.08, 16.54) * mm});
            skLineSegment(sketch, "E272", {"start": v(-423.08, 16.54) * mm, "end": v(-429.43, 16.54) * mm});
            skLineSegment(sketch, "E273", {"start": v(-429.43, 16.54) * mm, "end": v(-429.43, 10.19) * mm});
            skLineSegment(sketch, "E274", {"start": v(-429.43, 10.19) * mm, "end": v(-453.56, 10.19) * mm});
            skLineSegment(sketch, "E275", {"start": v(-453.56, 10.19) * mm, "end": v(-453.56, 22.89) * mm});
            skLineSegment(sketch, "E276", {"start": v(-453.56, 22.89) * mm, "end": v(-423.08, 22.89) * mm});
            skLineSegment(sketch, "E277", {"start": v(-423.08, 22.89) * mm, "end": v(-423.08, 40.67) * mm});
            skLineSegment(sketch, "E278", {"start": v(-423.08, 40.67) * mm, "end": v(-429.43, 40.67) * mm});
            skLineSegment(sketch, "E279", {"start": v(-429.43, 40.67) * mm, "end": v(-429.43, 34.32) * mm});
            skLineSegment(sketch, "E280", {"start": v(-429.43, 34.32) * mm, "end": v(-453.56, 34.32) * mm});
            skLineSegment(sketch, "E281", {"start": v(-453.56, 34.32) * mm, "end": v(-453.56, 47.02) * mm});
            skLineSegment(sketch, "E282", {"start": v(-377.36, -80.05) * mm, "end": v(-377.36, -73.63) * mm});
            skLineSegment(sketch, "E283", {"start": v(-377.36, -73.63) * mm, "end": v(-407.84, -73.63) * mm});
            skLineSegment(sketch, "E284", {"start": v(-407.84, -73.63) * mm, "end": v(-407.84, -55.85) * mm});
            skLineSegment(sketch, "E285", {"start": v(-407.84, -55.85) * mm, "end": v(-401.49, -55.85) * mm});
            skLineSegment(sketch, "E286", {"start": v(-401.49, -55.85) * mm, "end": v(-401.49, -62.2) * mm});
            skLineSegment(sketch, "E287", {"start": v(-401.49, -62.2) * mm, "end": v(-377.36, -62.2) * mm});
            skLineSegment(sketch, "E288", {"start": v(-377.36, -62.2) * mm, "end": v(-377.36, -49.5) * mm});
            skLineSegment(sketch, "E289", {"start": v(-377.36, -49.5) * mm, "end": v(-407.84, -49.5) * mm});
            skLineSegment(sketch, "E290", {"start": v(-407.84, -49.5) * mm, "end": v(-407.84, -31.72) * mm});
            skLineSegment(sketch, "E291", {"start": v(-407.84, -31.72) * mm, "end": v(-401.49, -31.72) * mm});
            skLineSegment(sketch, "E292", {"start": v(-401.49, -31.72) * mm, "end": v(-401.49, -38.07) * mm});
            skLineSegment(sketch, "E293", {"start": v(-401.49, -38.07) * mm, "end": v(-377.36, -38.07) * mm});
            skLineSegment(sketch, "E294", {"start": v(-377.36, -38.07) * mm, "end": v(-377.36, -25.37) * mm});
            skLineSegment(sketch, "E295", {"start": v(-377.36, -25.37) * mm, "end": v(-407.84, -25.37) * mm});
            skLineSegment(sketch, "E296", {"start": v(-407.84, -25.37) * mm, "end": v(-407.84, -7.6) * mm});
            skLineSegment(sketch, "E297", {"start": v(-407.84, -7.6) * mm, "end": v(-401.49, -7.6) * mm});
            skLineSegment(sketch, "E298", {"start": v(-401.49, -7.6) * mm, "end": v(-401.49, -13.94) * mm});
            skLineSegment(sketch, "E299", {"start": v(-401.49, -13.94) * mm, "end": v(-377.36, -13.94) * mm});
            skLineSegment(sketch, "E300", {"start": v(-377.36, -13.94) * mm, "end": v(-377.36, -1.24) * mm});
            skLineSegment(sketch, "E301", {"start": v(-377.36, -1.24) * mm, "end": v(-407.84, -1.24) * mm});
            skLineSegment(sketch, "E302", {"start": v(-407.84, -1.24) * mm, "end": v(-407.84, 16.54) * mm});
            skLineSegment(sketch, "E303", {"start": v(-407.84, 16.54) * mm, "end": v(-401.49, 16.54) * mm});
            skLineSegment(sketch, "E304", {"start": v(-401.49, 16.54) * mm, "end": v(-401.49, 10.19) * mm});
            skLineSegment(sketch, "E305", {"start": v(-401.49, 10.19) * mm, "end": v(-377.36, 10.19) * mm});
            skLineSegment(sketch, "E306", {"start": v(-377.36, 10.19) * mm, "end": v(-377.36, 22.89) * mm});
            skLineSegment(sketch, "E307", {"start": v(-377.36, 22.89) * mm, "end": v(-407.84, 22.89) * mm});
            skLineSegment(sketch, "E308", {"start": v(-407.84, 22.89) * mm, "end": v(-407.84, 40.67) * mm});
            skLineSegment(sketch, "E309", {"start": v(-407.84, 40.67) * mm, "end": v(-401.49, 40.67) * mm});
            skLineSegment(sketch, "E310", {"start": v(-401.49, 40.67) * mm, "end": v(-401.49, 34.32) * mm});
            skLineSegment(sketch, "E311", {"start": v(-401.49, 34.32) * mm, "end": v(-377.36, 34.32) * mm});
            skLineSegment(sketch, "E312", {"start": v(-377.36, 34.32) * mm, "end": v(-377.36, 47.02) * mm});
            skLineSegment(sketch, "E313", {"start": v(-423.08, -73.63) * mm, "end": v(-423.08, -55.85) * mm});
            skLineSegment(sketch, "E314", {"start": v(-429.43, -62.2) * mm, "end": v(-429.43, -55.85) * mm});
            skLineSegment(sketch, "E315", {"start": v(-429.43, -55.85) * mm, "end": v(-423.08, -55.85) * mm});
            skLineSegment(sketch, "E316", {"start": v(-423.08, -73.63) * mm, "end": v(-453.56, -73.63) * mm});
            skLineSegment(sketch, "E317", {"start": v(-453.56, -62.2) * mm, "end": v(-453.56, -49.5) * mm});
            skLineSegment(sketch, "E318", {"start": v(-453.56, -73.63) * mm, "end": v(-453.56, -80.05) * mm});
            skLineSegment(sketch, "E319", {"start": v(-453.56, -62.2) * mm, "end": v(-429.43, -62.2) * mm});
            skLineSegment(sketch, "E320", {"start": v(-453.56, -80.05) * mm, "end": v(-377.36, -80.05) * mm});
            skPoint(sketch, "E321", {"position": v(-415.46, -80.05) * mm});
            skLineSegment(sketch, "E322", {"start": v(-542.46, -49.5) * mm, "end": v(-511.98, -49.5) * mm});
            skLineSegment(sketch, "E323", {"start": v(-511.98, -49.5) * mm, "end": v(-511.98, -31.72) * mm});
            skLineSegment(sketch, "E324", {"start": v(-511.98, -31.72) * mm, "end": v(-518.33, -31.72) * mm});
            skLineSegment(sketch, "E325", {"start": v(-518.33, -31.72) * mm, "end": v(-518.33, -38.07) * mm});
            skLineSegment(sketch, "E326", {"start": v(-518.33, -38.07) * mm, "end": v(-542.46, -38.07) * mm});
            skLineSegment(sketch, "E327", {"start": v(-542.46, -38.07) * mm, "end": v(-542.46, -25.37) * mm});
            skLineSegment(sketch, "E328", {"start": v(-542.46, -25.37) * mm, "end": v(-511.98, -25.37) * mm});
            skLineSegment(sketch, "E329", {"start": v(-511.98, -25.37) * mm, "end": v(-511.98, -7.6) * mm});
            skLineSegment(sketch, "E330", {"start": v(-511.98, -7.6) * mm, "end": v(-518.33, -7.6) * mm});
            skLineSegment(sketch, "E331", {"start": v(-518.33, -7.6) * mm, "end": v(-518.33, -13.94) * mm});
            skLineSegment(sketch, "E332", {"start": v(-518.33, -13.94) * mm, "end": v(-542.46, -13.94) * mm});
            skLineSegment(sketch, "E333", {"start": v(-542.46, -13.94) * mm, "end": v(-542.46, -1.24) * mm});
            skLineSegment(sketch, "E334", {"start": v(-542.46, -1.24) * mm, "end": v(-511.98, -1.24) * mm});
            skLineSegment(sketch, "E335", {"start": v(-511.98, -1.24) * mm, "end": v(-511.98, 16.54) * mm});
            skLineSegment(sketch, "E336", {"start": v(-511.98, 16.54) * mm, "end": v(-518.33, 16.54) * mm});
            skLineSegment(sketch, "E337", {"start": v(-518.33, 16.54) * mm, "end": v(-518.33, 10.19) * mm});
            skLineSegment(sketch, "E338", {"start": v(-518.33, 10.19) * mm, "end": v(-542.46, 10.19) * mm});
            skLineSegment(sketch, "E339", {"start": v(-542.46, 10.19) * mm, "end": v(-542.46, 22.89) * mm});
            skLineSegment(sketch, "E340", {"start": v(-542.46, 22.89) * mm, "end": v(-511.98, 22.89) * mm});
            skLineSegment(sketch, "E341", {"start": v(-511.98, 22.89) * mm, "end": v(-511.98, 40.67) * mm});
            skLineSegment(sketch, "E342", {"start": v(-511.98, 40.67) * mm, "end": v(-518.33, 40.67) * mm});
            skLineSegment(sketch, "E343", {"start": v(-518.33, 40.67) * mm, "end": v(-518.33, 34.32) * mm});
            skLineSegment(sketch, "E344", {"start": v(-518.33, 34.32) * mm, "end": v(-542.46, 34.32) * mm});
            skLineSegment(sketch, "E345", {"start": v(-542.46, 34.32) * mm, "end": v(-542.46, 47.02) * mm});
            skLineSegment(sketch, "E346", {"start": v(-466.26, -80.05) * mm, "end": v(-466.26, -73.63) * mm});
            skLineSegment(sketch, "E347", {"start": v(-466.26, -73.63) * mm, "end": v(-496.74, -73.63) * mm});
            skLineSegment(sketch, "E348", {"start": v(-496.74, -73.63) * mm, "end": v(-496.74, -55.85) * mm});
            skLineSegment(sketch, "E349", {"start": v(-496.74, -55.85) * mm, "end": v(-490.39, -55.85) * mm});
            skLineSegment(sketch, "E350", {"start": v(-490.39, -55.85) * mm, "end": v(-490.39, -62.2) * mm});
            skLineSegment(sketch, "E351", {"start": v(-490.39, -62.2) * mm, "end": v(-466.26, -62.2) * mm});
            skLineSegment(sketch, "E352", {"start": v(-466.26, -62.2) * mm, "end": v(-466.26, -49.5) * mm});
            skLineSegment(sketch, "E353", {"start": v(-466.26, -49.5) * mm, "end": v(-496.74, -49.5) * mm});
            skLineSegment(sketch, "E354", {"start": v(-496.74, -49.5) * mm, "end": v(-496.74, -31.72) * mm});
            skLineSegment(sketch, "E355", {"start": v(-496.74, -31.72) * mm, "end": v(-490.39, -31.72) * mm});
            skLineSegment(sketch, "E356", {"start": v(-490.39, -31.72) * mm, "end": v(-490.39, -38.07) * mm});
            skLineSegment(sketch, "E357", {"start": v(-490.39, -38.07) * mm, "end": v(-466.26, -38.07) * mm});
            skLineSegment(sketch, "E358", {"start": v(-466.26, -38.07) * mm, "end": v(-466.26, -25.37) * mm});
            skLineSegment(sketch, "E359", {"start": v(-466.26, -25.37) * mm, "end": v(-496.74, -25.37) * mm});
            skLineSegment(sketch, "E360", {"start": v(-496.74, -25.37) * mm, "end": v(-496.74, -7.6) * mm});
            skLineSegment(sketch, "E361", {"start": v(-496.74, -7.6) * mm, "end": v(-490.39, -7.6) * mm});
            skLineSegment(sketch, "E362", {"start": v(-490.39, -7.6) * mm, "end": v(-490.39, -13.94) * mm});
            skLineSegment(sketch, "E363", {"start": v(-490.39, -13.94) * mm, "end": v(-466.26, -13.94) * mm});
            skLineSegment(sketch, "E364", {"start": v(-466.26, -13.94) * mm, "end": v(-466.26, -1.24) * mm});
            skLineSegment(sketch, "E365", {"start": v(-466.26, -1.24) * mm, "end": v(-496.74, -1.24) * mm});
            skLineSegment(sketch, "E366", {"start": v(-496.74, -1.24) * mm, "end": v(-496.74, 16.54) * mm});
            skLineSegment(sketch, "E367", {"start": v(-496.74, 16.54) * mm, "end": v(-490.39, 16.54) * mm});
            skLineSegment(sketch, "E368", {"start": v(-490.39, 16.54) * mm, "end": v(-490.39, 10.19) * mm});
            skLineSegment(sketch, "E369", {"start": v(-490.39, 10.19) * mm, "end": v(-466.26, 10.19) * mm});
            skLineSegment(sketch, "E370", {"start": v(-466.26, 10.19) * mm, "end": v(-466.26, 22.89) * mm});
            skLineSegment(sketch, "E371", {"start": v(-466.26, 22.89) * mm, "end": v(-496.74, 22.89) * mm});
            skLineSegment(sketch, "E372", {"start": v(-496.74, 22.89) * mm, "end": v(-496.74, 40.67) * mm});
            skLineSegment(sketch, "E373", {"start": v(-496.74, 40.67) * mm, "end": v(-490.39, 40.67) * mm});
            skLineSegment(sketch, "E374", {"start": v(-490.39, 40.67) * mm, "end": v(-490.39, 34.32) * mm});
            skLineSegment(sketch, "E375", {"start": v(-490.39, 34.32) * mm, "end": v(-466.26, 34.32) * mm});
            skLineSegment(sketch, "E376", {"start": v(-466.26, 34.32) * mm, "end": v(-466.26, 47.02) * mm});
            skLineSegment(sketch, "E377", {"start": v(-511.98, -73.63) * mm, "end": v(-511.98, -55.85) * mm});
            skLineSegment(sketch, "E378", {"start": v(-518.33, -62.2) * mm, "end": v(-518.33, -55.85) * mm});
            skLineSegment(sketch, "E379", {"start": v(-518.33, -55.85) * mm, "end": v(-511.98, -55.85) * mm});
            skLineSegment(sketch, "E380", {"start": v(-511.98, -73.63) * mm, "end": v(-542.46, -73.63) * mm});
            skLineSegment(sketch, "E381", {"start": v(-542.46, -62.2) * mm, "end": v(-542.46, -49.5) * mm});
            skLineSegment(sketch, "E382", {"start": v(-542.46, -73.63) * mm, "end": v(-542.46, -80.05) * mm});
            skLineSegment(sketch, "E383", {"start": v(-542.46, -62.2) * mm, "end": v(-518.33, -62.2) * mm});
            skLineSegment(sketch, "E384", {"start": v(-542.46, -80.05) * mm, "end": v(-466.26, -80.05) * mm});
            skPoint(sketch, "E385", {"position": v(-504.36, -80.05) * mm});
            skLineSegment(sketch, "E386", {"start": v(-542.46, 47.02) * mm, "end": v(-511.98, 47.02) * mm});
            skLineSegment(sketch, "E387", {"start": v(-511.98, 47.02) * mm, "end": v(-511.98, 64.8) * mm});
            skLineSegment(sketch, "E388", {"start": v(-511.98, 64.8) * mm, "end": v(-518.33, 64.8) * mm});
            skLineSegment(sketch, "E389", {"start": v(-518.33, 64.8) * mm, "end": v(-518.33, 58.45) * mm});
            skLineSegment(sketch, "E390", {"start": v(-518.33, 58.45) * mm, "end": v(-542.46, 58.45) * mm});
            skLineSegment(sketch, "E391", {"start": v(-542.46, 58.45) * mm, "end": v(-542.46, 71.15) * mm});
            skLineSegment(sketch, "E392", {"start": v(-542.46, 71.15) * mm, "end": v(-511.98, 71.15) * mm});
            skLineSegment(sketch, "E393", {"start": v(-511.98, 88.93) * mm, "end": v(-518.33, 88.93) * mm});
            skLineSegment(sketch, "E394", {"start": v(-518.33, 88.93) * mm, "end": v(-518.33, 82.58) * mm});
            skLineSegment(sketch, "E395", {"start": v(-518.33, 82.58) * mm, "end": v(-542.46, 82.58) * mm});
            skLineSegment(sketch, "E396", {"start": v(-542.46, 82.58) * mm, "end": v(-542.46, 95.28) * mm});
            skLineSegment(sketch, "E397", {"start": v(-466.26, 47.02) * mm, "end": v(-496.74, 47.02) * mm});
            skLineSegment(sketch, "E398", {"start": v(-496.74, 47.02) * mm, "end": v(-496.74, 64.8) * mm});
            skLineSegment(sketch, "E399", {"start": v(-496.74, 64.8) * mm, "end": v(-490.39, 64.8) * mm});
            skLineSegment(sketch, "E400", {"start": v(-490.39, 64.8) * mm, "end": v(-490.39, 58.45) * mm});
            skLineSegment(sketch, "E401", {"start": v(-490.39, 58.45) * mm, "end": v(-466.26, 58.45) * mm});
            skLineSegment(sketch, "E402", {"start": v(-466.26, 58.45) * mm, "end": v(-466.26, 71.15) * mm});
            skLineSegment(sketch, "E403", {"start": v(-466.26, 71.15) * mm, "end": v(-496.74, 71.15) * mm});
            skLineSegment(sketch, "E404", {"start": v(-496.74, 71.15) * mm, "end": v(-496.74, 88.93) * mm});
            skLineSegment(sketch, "E405", {"start": v(-496.74, 88.93) * mm, "end": v(-490.39, 88.93) * mm});
            skLineSegment(sketch, "E406", {"start": v(-490.39, 88.93) * mm, "end": v(-490.39, 82.58) * mm});
            skLineSegment(sketch, "E407", {"start": v(-490.39, 82.58) * mm, "end": v(-466.26, 82.58) * mm});
            skLineSegment(sketch, "E408", {"start": v(-466.26, 82.58) * mm, "end": v(-466.26, 95.28) * mm});
            skLineSegment(sketch, "E409", {"start": v(-511.98, 71.15) * mm, "end": v(-511.98, 88.93) * mm});
            skLineSegment(sketch, "E410", {"start": v(-542.46, 95.28) * mm, "end": v(-466.26, 95.28) * mm});
            skPoint(sketch, "E411", {"position": v(-504.36, 95.28) * mm});
            skLineSegment(sketch, "E412", {"start": v(-453.56, 47.02) * mm, "end": v(-423.08, 47.02) * mm});
            skLineSegment(sketch, "E413", {"start": v(-423.08, 47.02) * mm, "end": v(-423.08, 64.8) * mm});
            skLineSegment(sketch, "E414", {"start": v(-423.08, 64.8) * mm, "end": v(-429.43, 64.8) * mm});
            skLineSegment(sketch, "E415", {"start": v(-429.43, 64.8) * mm, "end": v(-429.43, 58.45) * mm});
            skLineSegment(sketch, "E416", {"start": v(-429.43, 58.45) * mm, "end": v(-453.56, 58.45) * mm});
            skLineSegment(sketch, "E417", {"start": v(-453.56, 58.45) * mm, "end": v(-453.56, 71.15) * mm});
            skLineSegment(sketch, "E418", {"start": v(-453.56, 71.15) * mm, "end": v(-423.08, 71.15) * mm});
            skLineSegment(sketch, "E419", {"start": v(-423.08, 88.93) * mm, "end": v(-429.43, 88.93) * mm});
            skLineSegment(sketch, "E420", {"start": v(-429.43, 88.93) * mm, "end": v(-429.43, 82.58) * mm});
            skLineSegment(sketch, "E421", {"start": v(-429.43, 82.58) * mm, "end": v(-453.56, 82.58) * mm});
            skLineSegment(sketch, "E422", {"start": v(-453.56, 82.58) * mm, "end": v(-453.56, 95.28) * mm});
            skLineSegment(sketch, "E423", {"start": v(-377.36, 47.02) * mm, "end": v(-407.84, 47.02) * mm});
            skLineSegment(sketch, "E424", {"start": v(-407.84, 47.02) * mm, "end": v(-407.84, 64.8) * mm});
            skLineSegment(sketch, "E425", {"start": v(-407.84, 64.8) * mm, "end": v(-401.49, 64.8) * mm});
            skLineSegment(sketch, "E426", {"start": v(-401.49, 64.8) * mm, "end": v(-401.49, 58.45) * mm});
            skLineSegment(sketch, "E427", {"start": v(-401.49, 58.45) * mm, "end": v(-377.36, 58.45) * mm});
            skLineSegment(sketch, "E428", {"start": v(-377.36, 58.45) * mm, "end": v(-377.36, 71.15) * mm});
            skLineSegment(sketch, "E429", {"start": v(-377.36, 71.15) * mm, "end": v(-407.84, 71.15) * mm});
            skLineSegment(sketch, "E430", {"start": v(-407.84, 71.15) * mm, "end": v(-407.84, 88.93) * mm});
            skLineSegment(sketch, "E431", {"start": v(-407.84, 88.93) * mm, "end": v(-401.49, 88.93) * mm});
            skLineSegment(sketch, "E432", {"start": v(-401.49, 88.93) * mm, "end": v(-401.49, 82.58) * mm});
            skLineSegment(sketch, "E433", {"start": v(-401.49, 82.58) * mm, "end": v(-377.36, 82.58) * mm});
            skLineSegment(sketch, "E434", {"start": v(-377.36, 82.58) * mm, "end": v(-377.36, 95.28) * mm});
            skLineSegment(sketch, "E435", {"start": v(-423.08, 71.15) * mm, "end": v(-423.08, 88.93) * mm});
            skLineSegment(sketch, "E436", {"start": v(-453.56, 95.28) * mm, "end": v(-377.36, 95.28) * mm});
            skPoint(sketch, "E437", {"position": v(-415.46, 95.28) * mm});
            skLineSegment(sketch, "E438", {"start": v(-364.66, 47.02) * mm, "end": v(-334.18, 47.02) * mm});
            skLineSegment(sketch, "E439", {"start": v(-334.18, 47.02) * mm, "end": v(-334.18, 64.8) * mm});
            skLineSegment(sketch, "E440", {"start": v(-334.18, 64.8) * mm, "end": v(-340.53, 64.8) * mm});
            skLineSegment(sketch, "E441", {"start": v(-340.53, 64.8) * mm, "end": v(-340.53, 58.45) * mm});
            skLineSegment(sketch, "E442", {"start": v(-340.53, 58.45) * mm, "end": v(-364.66, 58.45) * mm});
            skLineSegment(sketch, "E443", {"start": v(-364.66, 58.45) * mm, "end": v(-364.66, 71.15) * mm});
            skLineSegment(sketch, "E444", {"start": v(-364.66, 71.15) * mm, "end": v(-334.18, 71.15) * mm});
            skLineSegment(sketch, "E445", {"start": v(-334.18, 88.93) * mm, "end": v(-340.53, 88.93) * mm});
            skLineSegment(sketch, "E446", {"start": v(-340.53, 88.93) * mm, "end": v(-340.53, 82.58) * mm});
            skLineSegment(sketch, "E447", {"start": v(-340.53, 82.58) * mm, "end": v(-364.66, 82.58) * mm});
            skLineSegment(sketch, "E448", {"start": v(-364.66, 82.58) * mm, "end": v(-364.66, 95.28) * mm});
            skLineSegment(sketch, "E449", {"start": v(-288.46, 47.02) * mm, "end": v(-318.94, 47.02) * mm});
            skLineSegment(sketch, "E450", {"start": v(-318.94, 47.02) * mm, "end": v(-318.94, 64.8) * mm});
            skLineSegment(sketch, "E451", {"start": v(-318.94, 64.8) * mm, "end": v(-312.59, 64.8) * mm});
            skLineSegment(sketch, "E452", {"start": v(-312.59, 64.8) * mm, "end": v(-312.59, 58.45) * mm});
            skLineSegment(sketch, "E453", {"start": v(-312.59, 58.45) * mm, "end": v(-288.46, 58.45) * mm});
            skLineSegment(sketch, "E454", {"start": v(-288.46, 58.45) * mm, "end": v(-288.46, 71.15) * mm});
            skLineSegment(sketch, "E455", {"start": v(-288.46, 71.15) * mm, "end": v(-318.94, 71.15) * mm});
            skLineSegment(sketch, "E456", {"start": v(-318.94, 71.15) * mm, "end": v(-318.94, 88.93) * mm});
            skLineSegment(sketch, "E457", {"start": v(-318.94, 88.93) * mm, "end": v(-312.59, 88.93) * mm});
            skLineSegment(sketch, "E458", {"start": v(-312.59, 88.93) * mm, "end": v(-312.59, 82.58) * mm});
            skLineSegment(sketch, "E459", {"start": v(-312.59, 82.58) * mm, "end": v(-288.46, 82.58) * mm});
            skLineSegment(sketch, "E460", {"start": v(-288.46, 82.58) * mm, "end": v(-288.46, 95.28) * mm});
            skLineSegment(sketch, "E461", {"start": v(-334.18, 71.15) * mm, "end": v(-334.18, 88.93) * mm});
            skLineSegment(sketch, "E462", {"start": v(-364.66, 95.28) * mm, "end": v(-288.46, 95.28) * mm});
            skPoint(sketch, "E463", {"position": v(-326.56, 95.28) * mm});
            skLineSegment(sketch, "E464", {"start": v(-275.76, 47.02) * mm, "end": v(-245.28, 47.02) * mm});
            skLineSegment(sketch, "E465", {"start": v(-245.28, 47.02) * mm, "end": v(-245.28, 64.8) * mm});
            skLineSegment(sketch, "E466", {"start": v(-245.28, 64.8) * mm, "end": v(-251.63, 64.8) * mm});
            skLineSegment(sketch, "E467", {"start": v(-251.63, 64.8) * mm, "end": v(-251.63, 58.45) * mm});
            skLineSegment(sketch, "E468", {"start": v(-251.63, 58.45) * mm, "end": v(-275.76, 58.45) * mm});
            skLineSegment(sketch, "E469", {"start": v(-275.76, 58.45) * mm, "end": v(-275.76, 71.15) * mm});
            skLineSegment(sketch, "E470", {"start": v(-275.76, 71.15) * mm, "end": v(-245.28, 71.15) * mm});
            skLineSegment(sketch, "E471", {"start": v(-245.28, 88.93) * mm, "end": v(-251.63, 88.93) * mm});
            skLineSegment(sketch, "E472", {"start": v(-251.63, 88.93) * mm, "end": v(-251.63, 82.58) * mm});
            skLineSegment(sketch, "E473", {"start": v(-251.63, 82.58) * mm, "end": v(-275.76, 82.58) * mm});
            skLineSegment(sketch, "E474", {"start": v(-275.76, 82.58) * mm, "end": v(-275.76, 95.28) * mm});
            skLineSegment(sketch, "E475", {"start": v(-199.56, 47.02) * mm, "end": v(-230.04, 47.02) * mm});
            skLineSegment(sketch, "E476", {"start": v(-230.04, 47.02) * mm, "end": v(-230.04, 64.8) * mm});
            skLineSegment(sketch, "E477", {"start": v(-230.04, 64.8) * mm, "end": v(-223.69, 64.8) * mm});
            skLineSegment(sketch, "E478", {"start": v(-223.69, 64.8) * mm, "end": v(-223.69, 58.45) * mm});
            skLineSegment(sketch, "E479", {"start": v(-223.69, 58.45) * mm, "end": v(-199.56, 58.45) * mm});
            skLineSegment(sketch, "E480", {"start": v(-199.56, 58.45) * mm, "end": v(-199.56, 71.15) * mm});
            skLineSegment(sketch, "E481", {"start": v(-199.56, 71.15) * mm, "end": v(-230.04, 71.15) * mm});
            skLineSegment(sketch, "E482", {"start": v(-230.04, 71.15) * mm, "end": v(-230.04, 88.93) * mm});
            skLineSegment(sketch, "E483", {"start": v(-230.04, 88.93) * mm, "end": v(-223.69, 88.93) * mm});
            skLineSegment(sketch, "E484", {"start": v(-223.69, 88.93) * mm, "end": v(-223.69, 82.58) * mm});
            skLineSegment(sketch, "E485", {"start": v(-223.69, 82.58) * mm, "end": v(-199.56, 82.58) * mm});
            skLineSegment(sketch, "E486", {"start": v(-199.56, 82.58) * mm, "end": v(-199.56, 95.28) * mm});
            skLineSegment(sketch, "E487", {"start": v(-245.28, 71.15) * mm, "end": v(-245.28, 88.93) * mm});
            skLineSegment(sketch, "E488", {"start": v(-275.76, 95.28) * mm, "end": v(-199.56, 95.28) * mm});
            skPoint(sketch, "E489", {"position": v(-237.66, 95.28) * mm});
            skLineSegment(sketch, "E490", {"start": v(-186.86, 47.02) * mm, "end": v(-156.38, 47.02) * mm});
            skLineSegment(sketch, "E491", {"start": v(-156.38, 47.02) * mm, "end": v(-156.38, 64.8) * mm});
            skLineSegment(sketch, "E492", {"start": v(-156.38, 64.8) * mm, "end": v(-162.73, 64.8) * mm});
            skLineSegment(sketch, "E493", {"start": v(-162.73, 64.8) * mm, "end": v(-162.73, 58.45) * mm});
            skLineSegment(sketch, "E494", {"start": v(-162.73, 58.45) * mm, "end": v(-186.86, 58.45) * mm});
            skLineSegment(sketch, "E495", {"start": v(-186.86, 58.45) * mm, "end": v(-186.86, 71.15) * mm});
            skLineSegment(sketch, "E496", {"start": v(-186.86, 71.15) * mm, "end": v(-156.38, 71.15) * mm});
            skLineSegment(sketch, "E497", {"start": v(-156.38, 88.93) * mm, "end": v(-162.73, 88.93) * mm});
            skLineSegment(sketch, "E498", {"start": v(-162.73, 88.93) * mm, "end": v(-162.73, 82.58) * mm});
            skLineSegment(sketch, "E499", {"start": v(-162.73, 82.58) * mm, "end": v(-186.86, 82.58) * mm});
            skLineSegment(sketch, "E500", {"start": v(-186.86, 82.58) * mm, "end": v(-186.86, 95.28) * mm});
            skLineSegment(sketch, "E501", {"start": v(-110.66, 47.02) * mm, "end": v(-141.14, 47.02) * mm});
            skLineSegment(sketch, "E502", {"start": v(-141.14, 47.02) * mm, "end": v(-141.14, 64.8) * mm});
            skLineSegment(sketch, "E503", {"start": v(-141.14, 64.8) * mm, "end": v(-134.79, 64.8) * mm});
            skLineSegment(sketch, "E504", {"start": v(-134.79, 64.8) * mm, "end": v(-134.79, 58.45) * mm});
            skLineSegment(sketch, "E505", {"start": v(-134.79, 58.45) * mm, "end": v(-110.66, 58.45) * mm});
            skLineSegment(sketch, "E506", {"start": v(-110.66, 58.45) * mm, "end": v(-110.66, 71.15) * mm});
            skLineSegment(sketch, "E507", {"start": v(-110.66, 71.15) * mm, "end": v(-141.14, 71.15) * mm});
            skLineSegment(sketch, "E508", {"start": v(-141.14, 71.15) * mm, "end": v(-141.14, 88.93) * mm});
            skLineSegment(sketch, "E509", {"start": v(-141.14, 88.93) * mm, "end": v(-134.79, 88.93) * mm});
            skLineSegment(sketch, "E510", {"start": v(-134.79, 88.93) * mm, "end": v(-134.79, 82.58) * mm});
            skLineSegment(sketch, "E511", {"start": v(-134.79, 82.58) * mm, "end": v(-110.66, 82.58) * mm});
            skLineSegment(sketch, "E512", {"start": v(-110.66, 82.58) * mm, "end": v(-110.66, 95.28) * mm});
            skLineSegment(sketch, "E513", {"start": v(-156.38, 71.15) * mm, "end": v(-156.38, 88.93) * mm});
            skLineSegment(sketch, "E514", {"start": v(-186.86, 95.28) * mm, "end": v(-110.66, 95.28) * mm});
            skPoint(sketch, "E515", {"position": v(-148.76, 95.28) * mm});
            skLineSegment(sketch, "E516", {"start": v(-97.96, 47.02) * mm, "end": v(-67.48, 47.02) * mm});
            skLineSegment(sketch, "E517", {"start": v(-67.48, 47.02) * mm, "end": v(-67.48, 64.8) * mm});
            skLineSegment(sketch, "E518", {"start": v(-67.48, 64.8) * mm, "end": v(-73.83, 64.8) * mm});
            skLineSegment(sketch, "E519", {"start": v(-73.83, 64.8) * mm, "end": v(-73.83, 58.45) * mm});
            skLineSegment(sketch, "E520", {"start": v(-73.83, 58.45) * mm, "end": v(-97.96, 58.45) * mm});
            skLineSegment(sketch, "E521", {"start": v(-97.96, 58.45) * mm, "end": v(-97.96, 71.15) * mm});
            skLineSegment(sketch, "E522", {"start": v(-97.96, 71.15) * mm, "end": v(-67.48, 71.15) * mm});
            skLineSegment(sketch, "E523", {"start": v(-67.48, 88.93) * mm, "end": v(-73.83, 88.93) * mm});
            skLineSegment(sketch, "E524", {"start": v(-73.83, 88.93) * mm, "end": v(-73.83, 82.58) * mm});
            skLineSegment(sketch, "E525", {"start": v(-73.83, 82.58) * mm, "end": v(-97.96, 82.58) * mm});
            skLineSegment(sketch, "E526", {"start": v(-97.96, 82.58) * mm, "end": v(-97.96, 95.28) * mm});
            skLineSegment(sketch, "E527", {"start": v(-21.76, 47.02) * mm, "end": v(-52.24, 47.02) * mm});
            skLineSegment(sketch, "E528", {"start": v(-52.24, 47.02) * mm, "end": v(-52.24, 64.8) * mm});
            skLineSegment(sketch, "E529", {"start": v(-52.24, 64.8) * mm, "end": v(-45.89, 64.8) * mm});
            skLineSegment(sketch, "E530", {"start": v(-45.89, 64.8) * mm, "end": v(-45.89, 58.45) * mm});
            skLineSegment(sketch, "E531", {"start": v(-45.89, 58.45) * mm, "end": v(-21.76, 58.45) * mm});
            skLineSegment(sketch, "E532", {"start": v(-21.76, 58.45) * mm, "end": v(-21.76, 71.15) * mm});
            skLineSegment(sketch, "E533", {"start": v(-21.76, 71.15) * mm, "end": v(-52.24, 71.15) * mm});
            skLineSegment(sketch, "E534", {"start": v(-52.24, 71.15) * mm, "end": v(-52.24, 88.93) * mm});
            skLineSegment(sketch, "E535", {"start": v(-52.24, 88.93) * mm, "end": v(-45.89, 88.93) * mm});
            skLineSegment(sketch, "E536", {"start": v(-45.89, 88.93) * mm, "end": v(-45.89, 82.58) * mm});
            skLineSegment(sketch, "E537", {"start": v(-45.89, 82.58) * mm, "end": v(-21.76, 82.58) * mm});
            skLineSegment(sketch, "E538", {"start": v(-21.76, 82.58) * mm, "end": v(-21.76, 95.28) * mm});
            skLineSegment(sketch, "E539", {"start": v(-67.48, 71.15) * mm, "end": v(-67.48, 88.93) * mm});
            skLineSegment(sketch, "E540", {"start": v(-97.96, 95.28) * mm, "end": v(-21.76, 95.28) * mm});
            skPoint(sketch, "E541", {"position": v(-59.86, 95.28) * mm});
            skPoint(sketch, "E542", {"position": v(-282.1, 95.28) * mm});
            skSolve(sketch);
        }
        {
            var Q0;
            Q0=makeQuery(id+"F0.imprint","IMPRINT",FACE,{"disambiguationData":[TD([[makeQuery(id+"F0.imprint","IMPRINT",EDGE,{"derivedFrom":sQuery(id+"F0.wireOp",EDGE,"E0")}),1.0]])]});
            extrude(context, id + "F1", {"entities" : qUnion([Q0]), "depth" : 6.35 * mm});
        }
    });
